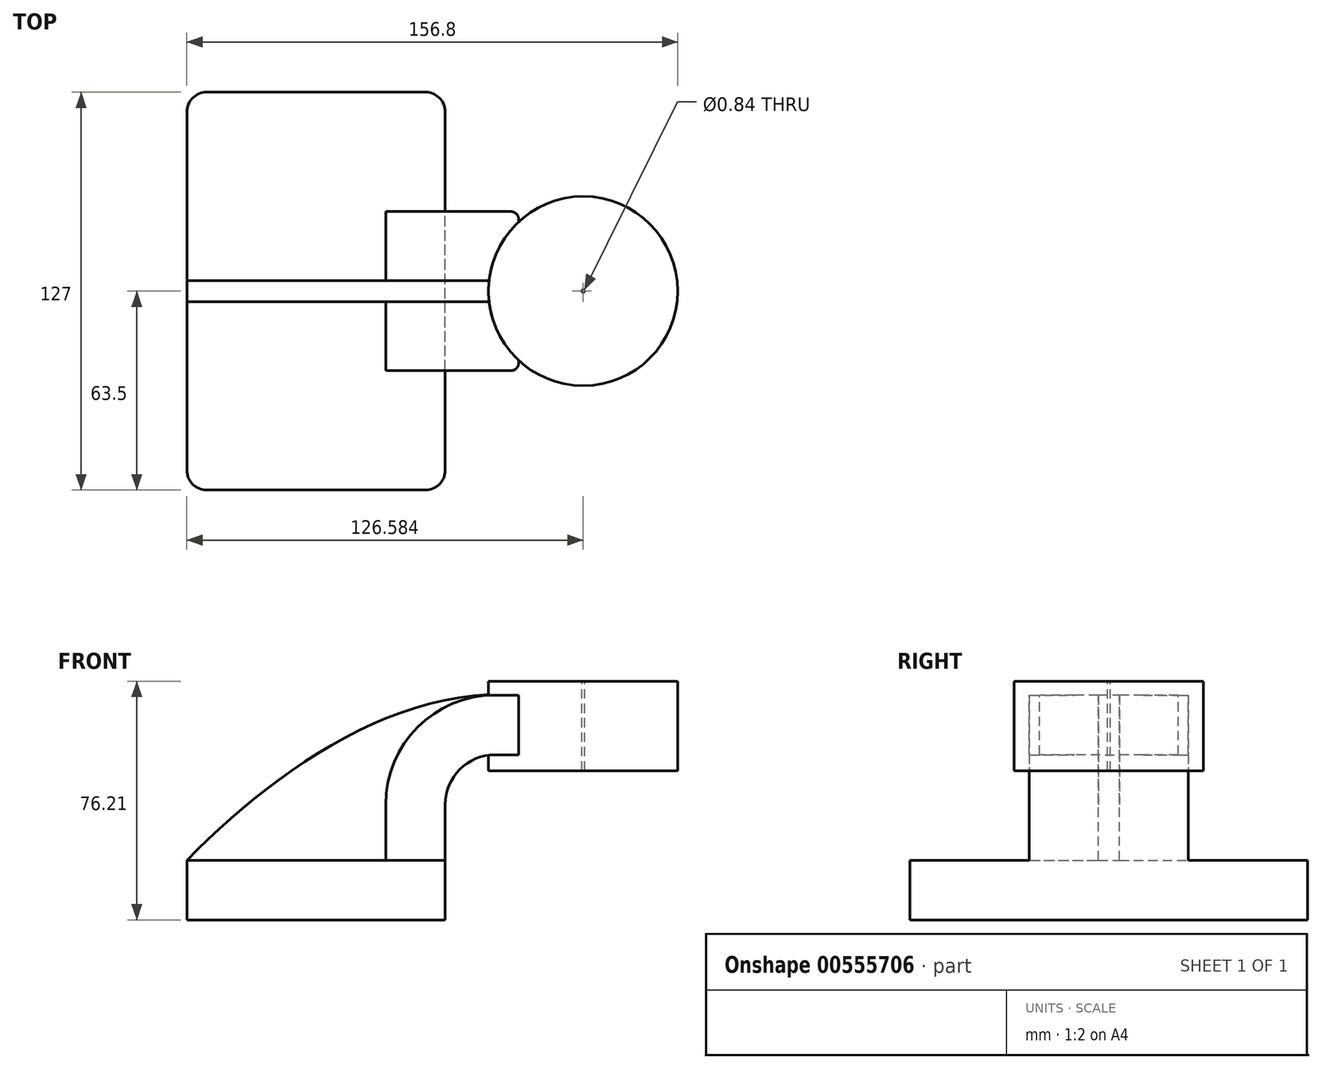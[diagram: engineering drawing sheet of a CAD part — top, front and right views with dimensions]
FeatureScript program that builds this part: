
annotation { "Feature Type Name" : "Feature", "Feature Type Description" : "" }
export const myFeature = defineFeature(function(context is Context, id is Id, definition is map)
    precondition{}
    {
        {
            var Q0;
            Q0=qCreatedBy(makeId("Front.planeOp"),FACE);
            var sketch = newSketch(context, id + "F0", { "sketchPlane" : qUnion([Q0])});
            skLineSegment(sketch, "E0.bottom", {"start": v(41.28, -9.52) * mm, "end": v(-41.28, -9.53) * mm});
            skLineSegment(sketch, "E0.top", {"start": v(41.28, 9.53) * mm, "end": v(-41.28, 9.53) * mm});
            skLineSegment(sketch, "E0.left", {"start": v(41.28, -9.52) * mm, "end": v(41.28, 9.53) * mm});
            skLineSegment(sketch, "E0.right", {"start": v(-41.28, -9.53) * mm, "end": v(-41.28, 9.53) * mm});
            skPoint(sketch, "E0.middle", {"position": v(0, 0) * mm});
            skLineSegment(sketch, "E1.bottom", {"start": v(115.52, 38.1) * mm, "end": v(64.72, 38.1) * mm});
            skLineSegment(sketch, "E1.top", {"start": v(115.52, 66.68) * mm, "end": v(64.72, 66.68) * mm});
            skLineSegment(sketch, "E1.left", {"start": v(115.52, 38.1) * mm, "end": v(115.52, 66.68) * mm});
            skLineSegment(sketch, "E1.right", {"start": v(64.72, 38.1) * mm, "end": v(64.72, 66.68) * mm});
            skPoint(sketch, "E1.middle", {"position": v(90.12, 52.39) * mm});
            skLineSegment(sketch, "E2", {"start": v(41.28, 9.53) * mm, "end": v(41.28, 27.3) * mm});
            skArc(sketch, "E3", {"start": v(57.15, 43.18) * mm, "mid": v(45.92, 38.53) * mm, "end": v(41.27, 27.3) * mm});
            skLineSegment(sketch, "E4", {"start": v(57.15, 43.18) * mm, "end": v(85.72, 43.18) * mm});
            skLineSegment(sketch, "E5.0", {"start": v(57.15, 62.23) * mm, "end": v(85.72, 62.23) * mm});
            skArc(sketch, "E5.1", {"start": v(57.15, 62.23) * mm, "mid": v(32.45, 52) * mm, "end": v(22.22, 27.3) * mm});
            skLineSegment(sketch, "E5.2", {"start": v(22.22, 9.53) * mm, "end": v(22.22, 27.3) * mm});
            skLineSegment(sketch, "E6", {"start": v(85.72, 62.23) * mm, "end": v(85.72, 43.18) * mm});
            skFitSpline(sketch, "E7", {"points": [v(-41.28, 9.53) * mm, v(64.72, 62.23) * mm], "startDerivative": vector(82.64, 83.31) * mm, "endDerivative": vector(121.01, -8.8) * mm});
            skLineSegment(sketch, "E8", {"start": v(85.72, 62.23) * mm, "end": v(85.72, 66.68) * mm});
            skLineSegment(sketch, "E9", {"start": v(85.72, 43.18) * mm, "end": v(85.72, 38.1) * mm});
            skSolve(sketch);
        }
        {
            var Q0;
            Q0=makeQuery(id+"F0.imprint","IMPRINT",FACE,{"disambiguationData":[TD([[makeQuery(id+"F0.imprint","IMPRINT",EDGE,{"derivedFrom":sQuery(id+"F0.wireOp",EDGE,"E0.bottom")}),-1.0]])]});
            extrude(context, id + "F1", {"entities" : qUnion([Q0]), "depth" : 127 * mm, "offsetDistance" : 25.4 * mm, "symmetric" : true});
        }
        {
            var Q0;
            {var subQ1=sQuery(id+"F0.wireOp",EDGE,"E2");Q0=makeQuery(id+"F0.imprint","IMPRINT",FACE,{"disambiguationData":[TD([[makeQuery(id+"F0.imprint","IMPRINT",EDGE,{"derivedFrom":subQ1}),1.0]])]});}
            extrude(context, id + "F2", {"entities" : qUnion([Q0]), "operationType" : NewBodyOperationType.ADD, "depth" : 50.8 * mm, "offsetDistance" : 25.4 * mm, "symmetric" : true});
        }
        {
            var Q0;
            {var subQ1=sQuery(id+"F0.wireOp",EDGE,"E5.1");Q0=makeQuery(id+"F0.imprint","IMPRINT",FACE,{"disambiguationData":[TD([[makeQuery(id+"F0.imprint","IMPRINT",EDGE,{"derivedFrom":subQ1}),-1.0]])]});}
            extrude(context, id + "F3", {"entities" : qUnion([Q0]), "operationType" : NewBodyOperationType.ADD, "depth" : 6.73 * mm, "offsetDistance" : 25.4 * mm, "symmetric" : true});
        }
        {
            var Q0;
            Q0=qCreatedBy(makeId("Front.planeOp"),FACE);
            var sketch = newSketch(context, id + "F4", { "sketchPlane" : qUnion([Q0])});
            skLineSegment(sketch, "E10", {"start": v(85.3, 67.18) * mm, "end": v(85.3, 37.93) * mm});
            skSolve(sketch);
        }
        {
            var Q0;
            {var subQ0=sQuery(id+"F0.wireOp",EDGE,"E1.left");Q0=makeQuery(id+"F0.imprint","IMPRINT",FACE,{"disambiguationData":[TD([[makeQuery(id+"F0.imprint","IMPRINT",EDGE,{"derivedFrom":subQ0}),1.0]])]});}
            var Q1;
            Q1=sQuery(id+"F4.wireOp",EDGE,"E10");
            revolve(context, id + "F5", {"operationType" : NewBodyOperationType.ADD, "entities" : qUnion([Q0]), "axis" : qUnion([Q1]), "revolveType" : RevolveType.FULL});
        }
        {
            var Q0;
            Q0=makeQuery(id+"F1.opExtrude","CAP_EDGE",EDGE,{"disambiguationData":[OSD([sQuery(id+"F0.wireOp",EDGE,"E0.right")])],"isStart":false});
            var Q1;
            Q1=makeQuery(id+"F1.opExtrude","CAP_EDGE",EDGE,{"disambiguationData":[OSD([sQuery(id+"F0.wireOp",EDGE,"E0.left")])],"isStart":false});
            var Q2;
            Q2=makeQuery(id+"F1.opExtrude","CAP_EDGE",EDGE,{"disambiguationData":[OSD([sQuery(id+"F0.wireOp",EDGE,"E0.left")])],"isStart":true});
            var Q3;
            Q3=makeQuery(id+"F1.opExtrude","CAP_EDGE",EDGE,{"disambiguationData":[OSD([sQuery(id+"F0.wireOp",EDGE,"E0.right")])],"isStart":true});
            fillet(context, id + "F6", {"entities" : qUnion([Q0, Q1, Q2, Q3]), "radius" : 6.35 * mm, "tangentPropagation" : true, "allowEdgeOverflow" : false});
        }
        {
            var Q0;
            Q0=makeQuery(id+"F2.opExtrude","CAP_EDGE",EDGE,{"disambiguationData":[OSD([sQuery(id+"F0.wireOp",EDGE,"E1.right")])],"isStart":false});
            fillet(context, id + "F7", {"entities" : qUnion([Q0]), "radius" : 2.54 * mm, "tangentPropagation" : true, "allowEdgeOverflow" : false});
        }
        {
            var Q0;
            Q0=makeQuery(id+"F2.opExtrude","CAP_EDGE",EDGE,{"disambiguationData":[OSD([sQuery(id+"F0.wireOp",EDGE,"E1.right")])],"isStart":true});
            fillet(context, id + "F8", {"entities" : qUnion([Q0]), "radius" : 2.54 * mm, "tangentPropagation" : true, "allowEdgeOverflow" : false});
        }
    });
